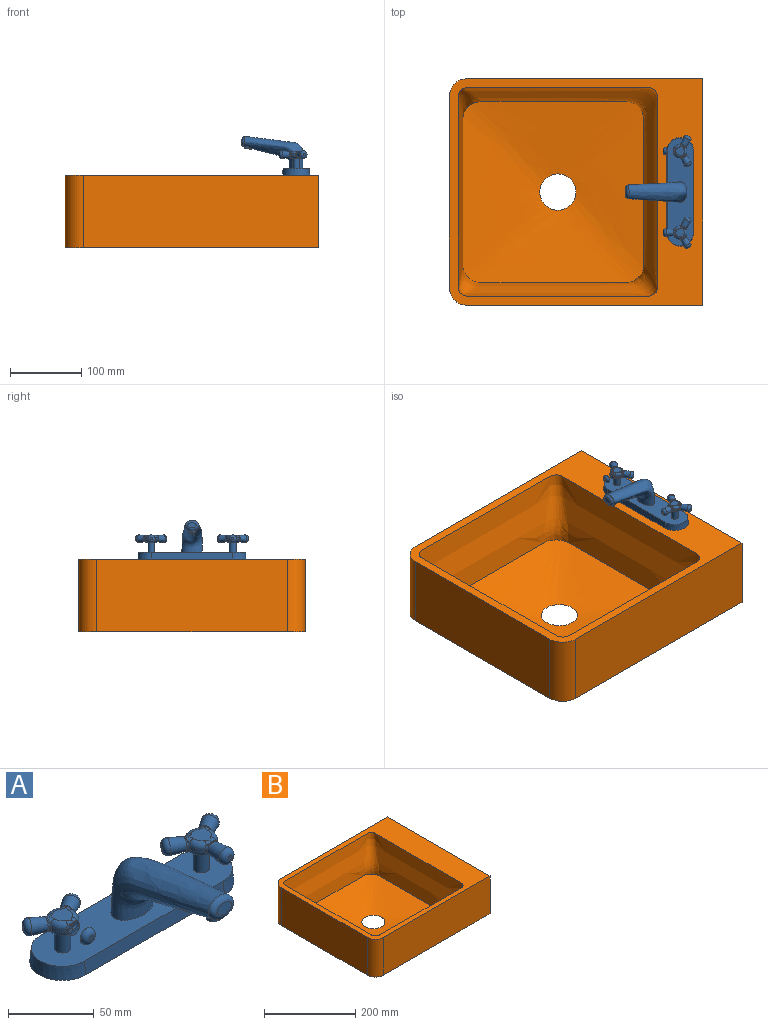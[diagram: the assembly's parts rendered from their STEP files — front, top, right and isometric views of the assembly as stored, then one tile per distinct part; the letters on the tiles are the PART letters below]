
ASSEMBLY  parts=2 mates=1
PART A: 137 faces, bbox 160x96.2x54.8 mm
  f0: cylinder r=9.53mm len=8.66mm, axis (0,0,1), area 20.3mm2, adj f89,f94,f104,f131
  f1: cylinder r=9.53mm len=7.5mm, axis (0,0,1), area 20.3mm2, adj f85,f97,f119,f128
  f2: cylinder r=9.53mm len=7.5mm, axis (0,0,1), area 20.3mm2, adj f88,f98,f107,f116
  f3: cylinder r=4.76mm len=14.29mm, axis (0,0,-1), area 427.5mm2, adj f7,f77
  f4: cylinder r=9.53mm len=7.5mm, axis (0,0,1), area 20.3mm2, adj f29,f35,f57,f72
  f5: cylinder r=9.53mm len=8.66mm, axis (0,0,1), area 20.3mm2, adj f26,f39,f48,f69
  f6: cylinder r=4.76mm len=14.29mm, axis (0,0,-1), area 427.5mm2, adj f7,f18
  f7: plane 150.84x36.54mm, normal (0,0,1), area 4636.8mm2, adj f3,f6,f8,f9,f10,f11,f13
  f8: cone r=19.05mm half-angle=5deg, axis (0,0,-1), area 559.7mm2, adj f7,f9,f11,f136
  f9: plane 114.3x9.53mm, normal (0,-1,0.09), area 1092.9mm2, adj f7,f8,f10,f136
  f10: cone r=19.05mm half-angle=5deg, axis (0,0,-1), area 559.7mm2, adj f7,f9,f11,f136
  f11: plane 114.3x9.53mm, normal (0,1,0.09), area 1092.9mm2, adj f7,f8,f10,f136
  f12: plane 12.2x7.4mm, normal (0,-0.99,0.12), area 69.4mm2, adj f16
  f13: bspline ~83.81x44.68mm, area 6377.7mm2, adj f7,f15,f16
  f14: plane 9.53x9.45mm, normal (0,-0.12,-0.99), area 71.3mm2, adj f15
  f15: cylinder r=4.76mm len=9.77mm, axis (0,-0.12,-0.99), area 54.6mm2, adj f13,f14
  f16: bspline ~19.44x14.97mm, area 250.1mm2, adj f12,f13
  f17: cylinder r=9.53mm len=7.5mm, axis (0,0,1), area 20.3mm2, adj f30,f38,f45,f60
  f18: plane 13.86x13.82mm, normal (0,0,-1), area 49.8mm2, adj f6,f35,f36,f37,f38,f39,f40
  f19: plane 13.86x13.82mm, normal (0,0,1), area 121.1mm2, adj f26,f27,f28,f29,f30,f31
  f20: cone r=3.57mm half-angle=5deg, axis (0,-1,0), area 314.9mm2, adj f32,f54,f55,f57,f58,f59,f60,f62
  f21: plane 3.41x3.41mm, normal (0,-1,0), area 9.1mm2, adj f32
  f22: plane 3.41x2.95mm, normal (-0.87,0.5,0), area 9.1mm2, adj f34
  f23: cone r=3.57mm half-angle=5deg, axis (-0.87,0.5,0), area 314.9mm2, adj f34,f66,f67,f69,f70,f71,f72,f74
  f24: cone r=3.57mm half-angle=5deg, axis (0.87,0.5,0), area 314.9mm2, adj f33,f42,f43,f45,f46,f47,f48,f50
  f25: plane 3.41x2.95mm, normal (0.87,0.5,0), area 9.1mm2, adj f33
  f26: torus R=5.91mm, axis (0,0,1), area 52.9mm2, adj f5,f19,f27,f28,f50,f71
  f27: bspline ~8.07x6.97mm, area 20.3mm2, adj f19,f26,f29,f73,f75,f76
  f28: bspline ~8.43x6.74mm, area 20.3mm2, adj f19,f26,f30,f49,f51,f52
  f29: torus R=5.91mm, axis (0,0,1), area 52.9mm2, adj f4,f19,f27,f31,f59,f74
  f30: torus R=5.91mm, axis (0,0,1), area 52.9mm2, adj f17,f19,f28,f31,f47,f62
  f31: bspline ~8.5x4.51mm, area 20.3mm2, adj f19,f29,f30,f61,f63,f64
  f32: torus R=1.71mm, axis (0,1,0), area 153.8mm2, adj f20,f21
  f33: torus R=1.71mm, axis (-0.87,-0.5,0), area 153.8mm2, adj f24,f25
  f34: torus R=1.71mm, axis (0.87,-0.5,0), area 153.8mm2, adj f22,f23
  f35: torus R=5.91mm, axis (0,0,1), area 52.9mm2, adj f4,f18,f36,f37,f55,f70
  f36: bspline ~8.5x4.51mm, area 20.3mm2, adj f18,f35,f38,f53,f54,f56
  f37: bspline ~8.43x6.74mm, area 20.3mm2, adj f18,f35,f39,f65,f66,f68
  f38: torus R=5.91mm, axis (0,0,1), area 52.9mm2, adj f17,f18,f36,f40,f43,f58
  f39: torus R=5.91mm, axis (0,0,1), area 52.9mm2, adj f5,f18,f37,f40,f46,f67
  f40: bspline ~8.07x6.97mm, area 20.3mm2, adj f18,f38,f39,f41,f42,f44
  f41: bspline ~1.33x1.07mm, area 0.1mm2, adj f40,f42,f43
  f42: bspline ~6.45x4.48mm, area 6.3mm2, adj f24,f40,f41,f44
  f43: bspline ~3.69x3mm, area 4.7mm2, adj f24,f38,f41,f45
  f44: bspline ~1.69x0.54mm, area 0.2mm2, adj f40,f42,f46
  f45: bspline ~5.01x2.05mm, area 3.9mm2, adj f17,f24,f43,f47
  f46: bspline ~3.69x2.54mm, area 4.7mm2, adj f24,f39,f44,f48
  f47: bspline ~3.69x3mm, area 4.7mm2, adj f24,f30,f45,f49
  f48: bspline ~5.01x2.37mm, area 3.9mm2, adj f5,f24,f46,f50
  f49: bspline ~1.33x1.07mm, area 0.2mm2, adj f28,f47,f51
  f50: bspline ~3.69x2.54mm, area 4.7mm2, adj f24,f26,f48,f52
  f51: bspline ~6.43x4.38mm, area 6.3mm2, adj f24,f28,f49,f52
  f52: bspline ~1.69x0.47mm, area 0.1mm2, adj f28,f50,f51
  f53: bspline ~1.59x0.64mm, area 0.1mm2, adj f36,f54,f55
  f54: bspline ~6.93x1.64mm, area 6.3mm2, adj f20,f36,f53,f56
  f55: bspline ~3.63x2.65mm, area 4.7mm2, adj f20,f35,f53,f57
  f56: bspline ~1.59x0.68mm, area 0.2mm2, adj f36,f54,f58
  f57: bspline ~4.01x2.06mm, area 3.9mm2, adj f4,f20,f55,f59
  f58: bspline ~3.63x2.65mm, area 4.7mm2, adj f20,f38,f56,f60
  f59: bspline ~3.63x2.65mm, area 4.7mm2, adj f20,f29,f57,f61
  f60: bspline ~5.01x2.06mm, area 3.9mm2, adj f17,f20,f58,f62
  f61: bspline ~1.59x0.68mm, area 0.2mm2, adj f31,f59,f63
  f62: bspline ~3.63x2.65mm, area 4.7mm2, adj f20,f30,f60,f64
  f63: bspline ~6.93x1.64mm, area 6.3mm2, adj f20,f31,f61,f64
  f64: bspline ~1.59x0.64mm, area 0.1mm2, adj f31,f62,f63
  f65: bspline ~1.69x0.47mm, area 0.1mm2, adj f37,f66,f67
  f66: bspline ~6.43x4.38mm, area 6.3mm2, adj f23,f37,f65,f68
  f67: bspline ~3.69x2.54mm, area 4.7mm2, adj f23,f39,f65,f69
  f68: bspline ~1.33x1.07mm, area 0.2mm2, adj f37,f66,f70
  f69: bspline ~5.01x2.37mm, area 3.9mm2, adj f5,f23,f67,f71
  f70: bspline ~3.69x3mm, area 4.7mm2, adj f23,f35,f68,f72
  f71: bspline ~3.69x2.54mm, area 4.7mm2, adj f23,f26,f69,f73
  f72: bspline ~5.01x2.05mm, area 3.9mm2, adj f4,f23,f70,f74
  f73: bspline ~1.69x0.54mm, area 0.2mm2, adj f27,f71,f75
  f74: bspline ~3.69x3mm, area 4.7mm2, adj f23,f29,f72,f76
  f75: bspline ~6.45x4.48mm, area 6.3mm2, adj f23,f27,f73,f76
  f76: bspline ~1.33x1.07mm, area 0.1mm2, adj f27,f74,f75
  f77: plane 13.86x13.82mm, normal (0,0,-1), area 49.8mm2, adj f3,f94,f95,f96,f97,f98,f99
  f78: plane 13.86x13.82mm, normal (0,0,1), area 121.1mm2, adj f85,f86,f87,f88,f89,f90
  f79: cone r=3.57mm half-angle=5deg, axis (0,-1,0), area 313.2mm2, adj f91,f113,f114,f116,f117,f118,f119,f121
  f80: plane 3.41x3.41mm, normal (0,-1,0), area 9.1mm2, adj f91
  f81: plane 3.41x2.95mm, normal (0.87,0.5,0), area 9.1mm2, adj f93
  f82: cone r=3.57mm half-angle=5deg, axis (0.87,0.5,0), area 314.9mm2, adj f93,f125,f126,f128,f129,f130,f131,f133
  f83: cone r=3.57mm half-angle=5deg, axis (-0.87,0.5,0), area 314.9mm2, adj f92,f101,f102,f104,f105,f106,f107,f109
  f84: plane 3.41x2.95mm, normal (-0.87,0.5,0), area 9.1mm2, adj f92
  f85: torus R=5.91mm, axis (0,0,1), area 52.9mm2, adj f1,f78,f86,f87,f121,f130
  f86: bspline ~8.5x4.51mm, area 20.3mm2, adj f78,f85,f88,f120,f122,f123
  f87: bspline ~8.07x6.97mm, area 20.3mm2, adj f78,f85,f89,f132,f134,f135
  f88: torus R=5.91mm, axis (0,0,1), area 52.9mm2, adj f2,f78,f86,f90,f109,f118
  f89: torus R=5.91mm, axis (0,0,1), area 52.9mm2, adj f0,f78,f87,f90,f106,f133
  f90: bspline ~8.43x6.74mm, area 20.3mm2, adj f78,f88,f89,f108,f110,f111
  f91: torus R=1.71mm, axis (0,1,0), area 153.8mm2, adj f79,f80
  f92: torus R=1.71mm, axis (0.87,-0.5,0), area 153.8mm2, adj f83,f84
  f93: torus R=1.71mm, axis (-0.87,-0.5,0), area 153.8mm2, adj f81,f82
  f94: torus R=5.91mm, axis (0,0,1), area 52.9mm2, adj f0,f77,f95,f96,f102,f129
  f95: bspline ~8.43x6.74mm, area 20.3mm2, adj f77,f94,f97,f124,f125,f127
  f96: bspline ~8.07x6.97mm, area 20.3mm2, adj f77,f94,f98,f100,f101,f103
  f97: torus R=5.91mm, axis (0,0,1), area 52.9mm2, adj f1,f77,f95,f99,f117,f126
  f98: torus R=5.91mm, axis (0,0,1), area 52.9mm2, adj f2,f77,f96,f99,f105,f114
  f99: bspline ~8.5x4.51mm, area 20.3mm2, adj f77,f97,f98,f112,f113,f115
  f100: bspline ~1.69x0.53mm, area 0.2mm2, adj f96,f101,f102
  f101: bspline ~6.46x4.48mm, area 6.4mm2, adj f83,f96,f100,f103
  f102: bspline ~3.69x2.54mm, area 4.7mm2, adj f83,f94,f100,f104
  f103: bspline ~1.33x1.07mm, area 0.2mm2, adj f96,f101,f105
  f104: bspline ~5.01x2.37mm, area 3.9mm2, adj f0,f83,f102,f106
  f105: bspline ~3.69x3mm, area 4.7mm2, adj f83,f98,f103,f107
  f106: bspline ~3.69x2.54mm, area 4.7mm2, adj f83,f89,f104,f108
  f107: bspline ~5.01x2.05mm, area 3.9mm2, adj f2,f83,f105,f109
  f108: bspline ~1.69x0.47mm, area 0.2mm2, adj f90,f106,f110
  f109: bspline ~3.69x3mm, area 4.7mm2, adj f83,f88,f107,f111
  f110: bspline ~6.43x4.38mm, area 6.4mm2, adj f83,f90,f108,f111
  f111: bspline ~1.33x1.07mm, area 0.2mm2, adj f90,f109,f110
  f112: bspline ~1.59x0.68mm, area 0.2mm2, adj f99,f113,f114
  f113: bspline ~7x1.68mm, area 6.4mm2, adj f79,f99,f112,f115
  f114: bspline ~3.63x2.65mm, area 4.7mm2, adj f79,f98,f112,f116
  f115: bspline ~1.59x0.64mm, area 0.2mm2, adj f99,f113,f117
  f116: bspline ~5.01x2.06mm, area 3.9mm2, adj f2,f79,f114,f118
  f117: bspline ~3.63x2.65mm, area 4.7mm2, adj f79,f97,f115,f119
  f118: bspline ~3.63x2.65mm, area 4.7mm2, adj f79,f88,f116,f120
  f119: bspline ~5.01x2.06mm, area 3.9mm2, adj f1,f79,f117,f121
  f120: bspline ~1.59x0.64mm, area 0.2mm2, adj f86,f118,f122
  f121: bspline ~3.63x2.65mm, area 4.7mm2, adj f79,f85,f119,f123
  f122: bspline ~7x1.68mm, area 6.4mm2, adj f79,f86,f120,f123
  f123: bspline ~1.59x0.68mm, area 0.2mm2, adj f86,f121,f122
  f124: bspline ~1.33x1.07mm, area 0.2mm2, adj f95,f125,f126
  f125: bspline ~6.43x4.38mm, area 6.4mm2, adj f82,f95,f124,f127
  f126: bspline ~3.69x3mm, area 4.7mm2, adj f82,f97,f124,f128
  f127: bspline ~1.69x0.47mm, area 0.2mm2, adj f95,f125,f129
  f128: bspline ~5.01x2.05mm, area 3.9mm2, adj f1,f82,f126,f130
  f129: bspline ~3.69x2.54mm, area 4.7mm2, adj f82,f94,f127,f131
  f130: bspline ~3.69x3mm, area 4.7mm2, adj f82,f85,f128,f132
  f131: bspline ~5.01x2.37mm, area 3.9mm2, adj f0,f82,f129,f133
  f132: bspline ~1.33x1.07mm, area 0.2mm2, adj f87,f130,f134
  f133: bspline ~3.69x2.54mm, area 4.7mm2, adj f82,f89,f131,f135
  f134: bspline ~6.46x4.48mm, area 6.4mm2, adj f82,f87,f132,f135
  f135: bspline ~1.69x0.53mm, area 0.2mm2, adj f87,f133,f134
  f136: plane 152.4x38.1mm, normal (0,0,-1), area 5494.9mm2, adj f8,f9,f10,f11
PART B: 10 faces, bbox 356.9x318.8x102.9 mm
  f0: plane 356.94x318.84mm, normal (0,0,-1), area 110599.4mm2, adj f1,f2,f3,f4,f5,f8,f9
  f1: cylinder r=25.4mm len=101.6mm, axis (0,0,1), area 4053.7mm2, adj f0,f2,f5,f6
  f2: plane 330.2x101.6mm, normal (0,-1,0), area 33548.3mm2, adj f0,f1,f6,f9
  f3: plane 330.2x101.6mm, normal (0,1,0), area 33548.3mm2, adj f0,f4,f6,f9
  f4: cylinder r=25.4mm len=101.6mm, axis (0,0,1), area 4053.7mm2, adj f0,f3,f5,f6
  f5: plane 266.7x101.6mm, normal (-1,0,0), area 27096.7mm2, adj f0,f1,f4,f6
  f6: plane 356.87x318.77mm, normal (0,0,1), area 31152.3mm2, adj f1,f2,f3,f4,f5,f7,f9
  f7: bspline ~292.1x279.4mm, area 95181.9mm2, adj f6,f8
  f8: bspline ~254x254mm, area 62343.9mm2, adj f0,f7
  f9: plane 317.5x101.6mm, normal (1,0,0), area 32258mm2, adj f0,f2,f3,f6
PLACE A rot(axis=(0,0,-1),90deg) t=(-197.37,-4.4,-33.59)mm
PLACE B t=(-162.15,-84.41,42.61)mm
MATE fastened A.f136 <-> B.f6  axis (0,0,-1) through (9.3,-84.41,42.61)mm
